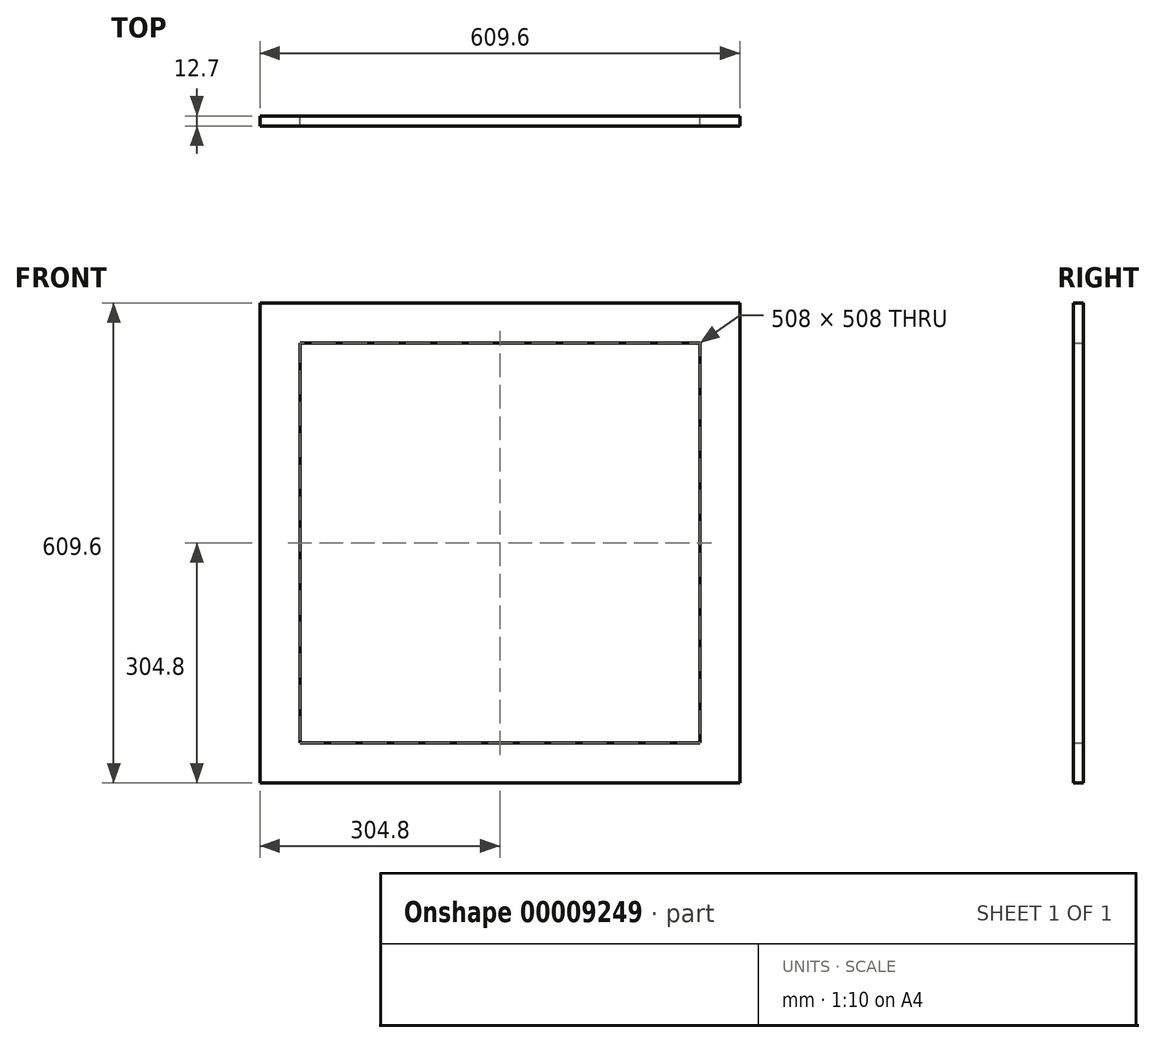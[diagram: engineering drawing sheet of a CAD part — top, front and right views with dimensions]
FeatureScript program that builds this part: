
annotation { "Feature Type Name" : "Feature", "Feature Type Description" : "" }
export const myFeature = defineFeature(function(context is Context, id is Id, definition is map)
    precondition{}
    {
        {
            var Q0;
            Q0=qCreatedBy(makeId("Front.planeOp"),FACE);
            var sketch = newSketch(context, id + "F0", { "sketchPlane" : qUnion([Q0])});
            skLineSegment(sketch, "E0.rect.bottom", {"start": v(304.8, 304.8) * mm, "end": v(-304.8, 304.8) * mm});
            skLineSegment(sketch, "E0.rect.top", {"start": v(304.8, -304.8) * mm, "end": v(-304.8, -304.8) * mm});
            skLineSegment(sketch, "E0.rect.left", {"start": v(304.8, 304.8) * mm, "end": v(304.8, -304.8) * mm});
            skLineSegment(sketch, "E0.rect.right", {"start": v(-304.8, 304.8) * mm, "end": v(-304.8, -304.8) * mm});
            skPoint(sketch, "E0.rect.middle", {"position": v(0, 0) * mm});
            skLineSegment(sketch, "E1.rect.bottom", {"start": v(254, -254) * mm, "end": v(-254, -254) * mm});
            skLineSegment(sketch, "E1.rect.top", {"start": v(254, 254) * mm, "end": v(-254, 254) * mm});
            skLineSegment(sketch, "E1.rect.left", {"start": v(254, -254) * mm, "end": v(254, 254) * mm});
            skLineSegment(sketch, "E1.rect.right", {"start": v(-254, -254) * mm, "end": v(-254, 254) * mm});
            skSolve(sketch);
        }
        {
            var Q0;
            Q0=makeQuery(id+"F0.imprint","IMPRINT",FACE,{"disambiguationData":[TD([[makeQuery(id+"F0.imprint","IMPRINT",EDGE,{"derivedFrom":sQuery(id+"F0.wireOp",EDGE,"E0.rect.bottom")}),1.0]])]});
            extrude(context, id + "F1", {"entities" : qUnion([Q0]), "depth" : 12.7 * mm});
        }
    });
